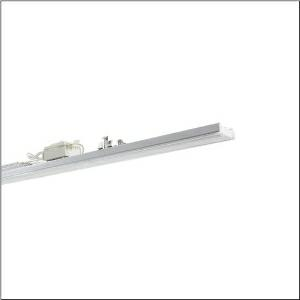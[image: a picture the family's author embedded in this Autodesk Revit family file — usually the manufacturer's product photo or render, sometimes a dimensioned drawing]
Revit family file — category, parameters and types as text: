
# Revit family: licross_r__11_recessed_mo_51tl12dn455g_7c9c
name_source: partatom
category: Lighting Fixtures
units: mm (PartAtom-declared; Revit-internal decimal feet)

## family parameters
Cut with Voids When Loaded = No
Host = Face
Light Source = No
Part Type = Normal
Room Calculation Point = No
Round Connector Dimension = Use Diameter
Shared = No

## types (1)
- --- (1 x LED, 5700 lm, 29.9 W, 4000K)
    Apparent Load = 30 VA
    CIE Flux Codes = 67 92 99 100 100
    Color Rendering = 80
    Color Temperature = 4000K
    Default Elevation = 1800 mm
    Description = Licross® 11 Recessed MO, luminaire insert, of sheet steel, coil coated, white, length: 1.500mm, width: 66mm, height: 67mm, LED rated luminous flux: 5.700lm, light colour: 840, control gear: DALI 2, with plug, 5-pole, with phase selection, mains connection: 220..240V, AC, 50/60Hz, rated input power: 30W, internal wiring halogen-free, primary optical cover: cover, of PMMA, light emission: direct distribution, primary light characteristic: symmetric, protection rating (complete): IP40, insulation class (complete): insulation class I (protective earthing), certification: CE, ENEC, VDE, UKCA, protection symbol: D if used in an environment without relevant dust loads with corresponding accessories, impact resistance: IK06, permissible ambient temperature for indoor applications: -25..+45°C, corresponds to IFS (International Featured Standards) requirements for safety and quality in the food industry, reducing of maximum allowable ambient temperature of 5°C with ceiling mounting, LABS conformity tested according to VDMA 24364:2018-05, packaging unit: 1 piece
    Height = 58 mm
    Lamp = 1 x LED
    Lamp Light Flux = 5700 lm
    Lamp Power = 29.9 W
    Lamp count = 1
    Length = 1500 mm
    Luminous efficacy = 191 lm/W
    Manufacturer = Siteco
    ModVariant = No
    Model = 51TL12DN455G
    Mounting Place = Ceiling
    Mounting Type = Pendant
    Number of Poles = 1
    OnlyDefault = Yes
    Power Factor = 1
    Product Name = Licross® 11 Recessed MO
    Product group = luminaire insert | ceiling pendant
    ProductGroupID = 902
    Protection Class = Protection class I
    Protection Degree = IP 40
    RLX_Detail_Level = 1
    RLX_Emergency_Light_Flux = 0 lm
    RLX_Emergency_Type = 0
    RLX_Emergency_Type_DB = No
    RlxData = <blob elided: 24017 chars, md5=4f779874>
    Socket = socket
    Standby Power = 0 W
    System Light Flux = 5700 lm
    System Power = 30 W
    Type Comments = factory setting: luminous flux: 100 % | dim-lin: 254 | 202 mA
    Type Image = l_1296930.jpg
    URL = http://relux.com
    VarID = @adj_121703
    Voltage = 0 V
    Weight = 0.00 kg
    Width = 66 mm

## geometry (parser evidence)
native form markers: Blend x4, Sweep x12
no freeform markers — native parametric forms only
